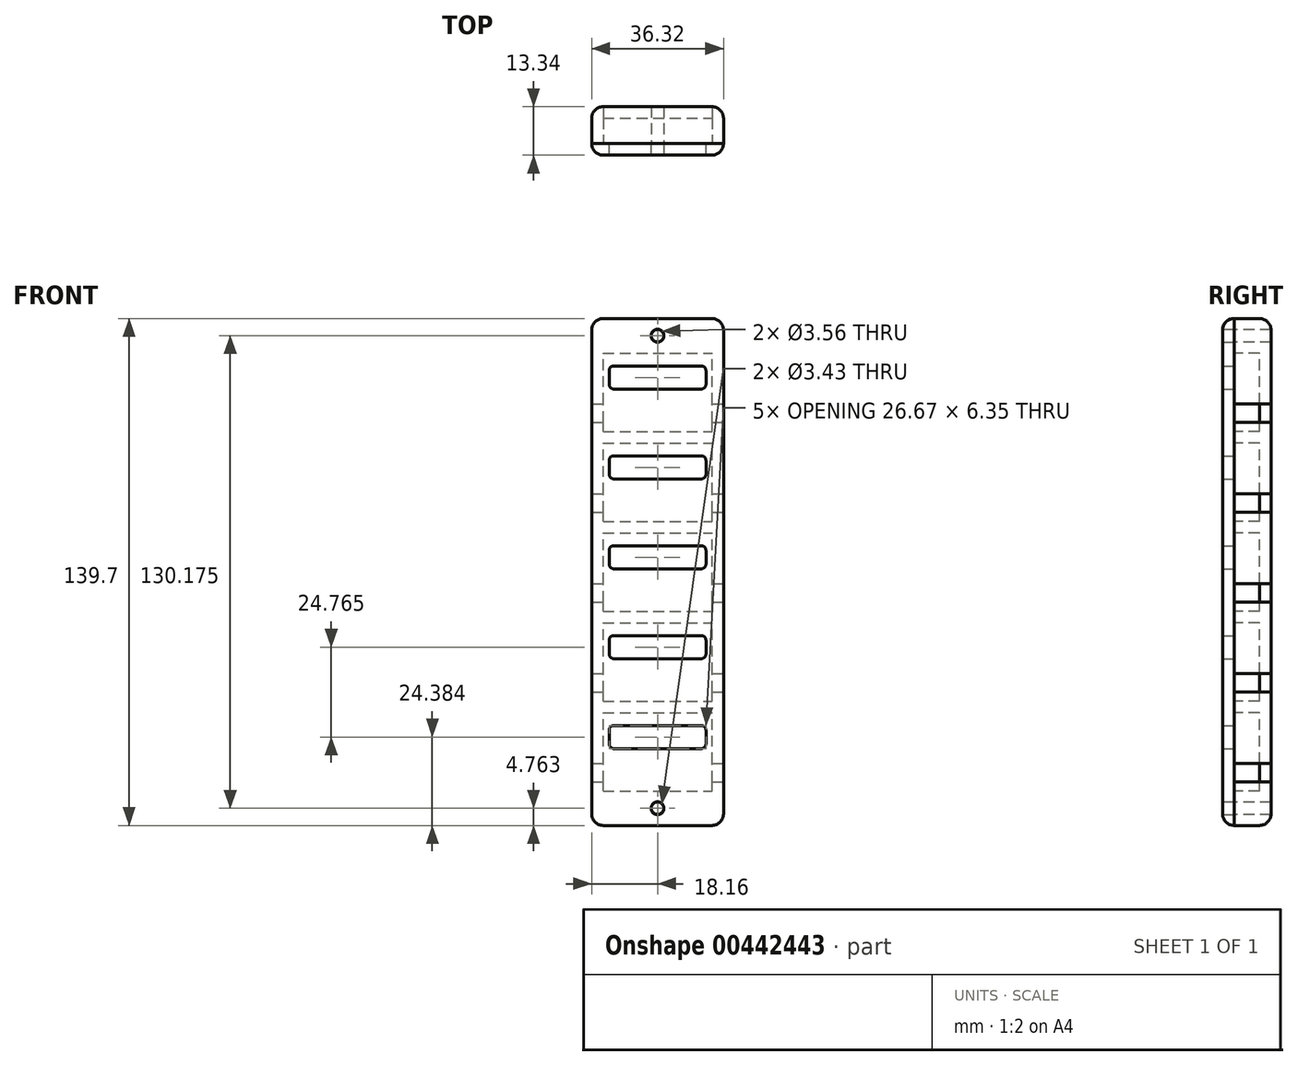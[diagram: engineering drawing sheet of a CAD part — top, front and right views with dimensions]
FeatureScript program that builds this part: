
annotation { "Feature Type Name" : "Feature", "Feature Type Description" : "" }
export const myFeature = defineFeature(function(context is Context, id is Id, definition is map)
    precondition{}
    {
        {
            var Q0;
            Q0=qCreatedBy(makeId("Front.planeOp"),FACE);
            var sketch = newSketch(context, id + "F0", { "sketchPlane" : qUnion([Q0])});
            skLineSegment(sketch, "E0.bottom", {"start": v(-18.16, 0) * mm, "end": v(18.16, 0) * mm});
            skLineSegment(sketch, "E0.top", {"start": v(-18.16, 139.7) * mm, "end": v(18.16, 139.7) * mm});
            skLineSegment(sketch, "E0.left", {"start": v(-18.16, 0) * mm, "end": v(-18.16, 139.7) * mm});
            skLineSegment(sketch, "E0.right", {"start": v(18.16, 0) * mm, "end": v(18.16, 139.7) * mm});
            skLineSegment(sketch, "E1.bottom", {"start": v(-14.99, 9.53) * mm, "end": v(14.99, 9.53) * mm});
            skLineSegment(sketch, "E1.top", {"start": v(-14.99, 31.12) * mm, "end": v(14.99, 31.12) * mm});
            skLineSegment(sketch, "E1.left", {"start": v(-14.99, 9.53) * mm, "end": v(-14.99, 31.12) * mm});
            skLineSegment(sketch, "E1.right", {"start": v(14.99, 9.53) * mm, "end": v(14.99, 31.12) * mm});
            skLineSegment(sketch, "E2.bottom", {"start": v(-14.99, 34.3) * mm, "end": v(14.99, 34.3) * mm});
            skLineSegment(sketch, "E2.top", {"start": v(-14.99, 55.88) * mm, "end": v(14.99, 55.88) * mm});
            skLineSegment(sketch, "E2.left", {"start": v(-14.99, 34.3) * mm, "end": v(-14.99, 55.88) * mm});
            skLineSegment(sketch, "E2.right", {"start": v(14.99, 34.3) * mm, "end": v(14.99, 55.88) * mm});
            skLineSegment(sketch, "E3.bottom", {"start": v(-14.99, 59.06) * mm, "end": v(14.99, 59.06) * mm});
            skLineSegment(sketch, "E3.top", {"start": v(-14.99, 80.65) * mm, "end": v(14.99, 80.65) * mm});
            skLineSegment(sketch, "E3.left", {"start": v(-14.99, 59.06) * mm, "end": v(-14.99, 80.65) * mm});
            skLineSegment(sketch, "E3.right", {"start": v(14.99, 59.06) * mm, "end": v(14.99, 80.65) * mm});
            skLineSegment(sketch, "E4.bottom", {"start": v(-14.99, 83.82) * mm, "end": v(14.99, 83.82) * mm});
            skLineSegment(sketch, "E4.top", {"start": v(-14.99, 105.41) * mm, "end": v(14.99, 105.41) * mm});
            skLineSegment(sketch, "E4.left", {"start": v(-14.99, 83.82) * mm, "end": v(-14.99, 105.41) * mm});
            skLineSegment(sketch, "E4.right", {"start": v(14.99, 83.82) * mm, "end": v(14.99, 105.41) * mm});
            skLineSegment(sketch, "E5.bottom", {"start": v(-14.99, 108.59) * mm, "end": v(14.99, 108.59) * mm});
            skLineSegment(sketch, "E5.top", {"start": v(-14.99, 130.18) * mm, "end": v(14.99, 130.18) * mm});
            skLineSegment(sketch, "E5.left", {"start": v(-14.99, 108.59) * mm, "end": v(-14.99, 130.18) * mm});
            skLineSegment(sketch, "E5.right", {"start": v(14.99, 108.59) * mm, "end": v(14.99, 130.18) * mm});
            skLineSegment(sketch, "E6", {"start": v(-18.16, 14.6) * mm, "end": v(18.16, 14.6) * mm, "construction": true});
            skLineSegment(sketch, "E7.bottom", {"start": v(-18.16, 12.06) * mm, "end": v(18.16, 12.06) * mm});
            skLineSegment(sketch, "E7.top", {"start": v(-18.16, 17.14) * mm, "end": v(18.16, 17.14) * mm});
            skLineSegment(sketch, "E7.left", {"start": v(-18.16, 12.06) * mm, "end": v(-18.16, 17.14) * mm});
            skLineSegment(sketch, "E7.right", {"start": v(18.16, 12.06) * mm, "end": v(18.16, 17.14) * mm});
            skLineSegment(sketch, "E8.0.1.0", {"start": v(-18.16, 36.83) * mm, "end": v(18.16, 36.83) * mm});
            skLineSegment(sketch, "E8.0.1.1", {"start": v(-18.16, 41.91) * mm, "end": v(18.16, 41.91) * mm});
            skLineSegment(sketch, "E8.0.1.2", {"start": v(18.16, 36.83) * mm, "end": v(18.16, 41.91) * mm});
            skLineSegment(sketch, "E8.0.1.3", {"start": v(-18.16, 39.37) * mm, "end": v(18.16, 39.37) * mm, "construction": true});
            skLineSegment(sketch, "E8.0.1.4", {"start": v(-18.16, 36.83) * mm, "end": v(-18.16, 41.91) * mm});
            skLineSegment(sketch, "E8.0.2.0", {"start": v(-18.16, 61.6) * mm, "end": v(18.16, 61.6) * mm});
            skLineSegment(sketch, "E8.0.2.1", {"start": v(-18.16, 66.67) * mm, "end": v(18.16, 66.67) * mm});
            skLineSegment(sketch, "E8.0.2.2", {"start": v(18.16, 61.6) * mm, "end": v(18.16, 66.67) * mm});
            skLineSegment(sketch, "E8.0.2.3", {"start": v(-18.16, 64.13) * mm, "end": v(18.16, 64.13) * mm, "construction": true});
            skLineSegment(sketch, "E8.0.2.4", {"start": v(-18.16, 61.6) * mm, "end": v(-18.16, 66.67) * mm});
            skLineSegment(sketch, "E8.0.3.0", {"start": v(-18.16, 86.36) * mm, "end": v(18.16, 86.36) * mm});
            skLineSegment(sketch, "E8.0.3.1", {"start": v(-18.16, 91.44) * mm, "end": v(18.16, 91.44) * mm});
            skLineSegment(sketch, "E8.0.3.2", {"start": v(18.16, 86.36) * mm, "end": v(18.16, 91.44) * mm});
            skLineSegment(sketch, "E8.0.3.3", {"start": v(-18.16, 88.9) * mm, "end": v(18.16, 88.9) * mm, "construction": true});
            skLineSegment(sketch, "E8.0.3.4", {"start": v(-18.16, 86.36) * mm, "end": v(-18.16, 91.44) * mm});
            skLineSegment(sketch, "E8.0.4.0", {"start": v(-18.16, 111.12) * mm, "end": v(18.16, 111.12) * mm});
            skLineSegment(sketch, "E8.0.4.1", {"start": v(-18.16, 116.2) * mm, "end": v(18.16, 116.2) * mm});
            skLineSegment(sketch, "E8.0.4.2", {"start": v(18.16, 111.12) * mm, "end": v(18.16, 116.2) * mm});
            skLineSegment(sketch, "E8.0.4.3", {"start": v(-18.16, 113.66) * mm, "end": v(18.16, 113.66) * mm, "construction": true});
            skLineSegment(sketch, "E8.0.4.4", {"start": v(-18.16, 111.12) * mm, "end": v(-18.16, 116.2) * mm});
            skLineSegment(sketch, "E8.direction1", {"start": v(-18.16, 12.06) * mm, "end": v(7.24, 12.06) * mm, "construction": true});
            skLineSegment(sketch, "E8.direction2", {"start": v(-18.16, 12.06) * mm, "end": v(-18.16, 36.83) * mm, "construction": true});
            skLineSegment(sketch, "E9", {"start": v(0, 139.7) * mm, "end": v(0, 130.18) * mm, "construction": true});
            skCircle(sketch, "E10", {"center": v(0, 134.94) * mm, "radius": 1.71 * mm});
            skLineSegment(sketch, "E11", {"start": v(0, 9.53) * mm, "end": v(0, 0) * mm, "construction": true});
            skCircle(sketch, "E12", {"center": v(0, 4.76) * mm, "radius": 1.71 * mm});
            skSolve(sketch);
        }
        {
            var Q0;
            {var subQ0=sQuery(id+"F0.wireOp",EDGE,"E7.bottom");var subQ1=sQuery(id+"F0.wireOp",EDGE,"E1.left");var subQ2=makeQuery(id+"F0.imprint","INTERSECT",VERTEX,{"derivedFrom":[subQ1,subQ0]});Q0=makeQuery(id+"F0.imprint","IMPRINT",FACE,{"disambiguationData":[TD([[makeQuery(id+"F0.imprint","IMPRINT",EDGE,{"disambiguationData":[TD([[subQ2,-1.0]])],"derivedFrom":subQ1}),-1.0]])]});}
            var Q1;
            {var subQ12=sQuery(id+"F0.wireOp",EDGE,"E3.top");Q1=makeQuery(id+"F0.imprint","IMPRINT",FACE,{"disambiguationData":[TD([[makeQuery(id+"F0.imprint","IMPRINT",EDGE,{"derivedFrom":subQ12}),1.0]])]});}
            var Q2;
            {var subQ0=sQuery(id+"F0.wireOp",EDGE,"E3.bottom");Q2=makeQuery(id+"F0.imprint","IMPRINT",FACE,{"disambiguationData":[TD([[makeQuery(id+"F0.imprint","IMPRINT",EDGE,{"derivedFrom":subQ0}),1.0]])]});}
            var Q3;
            {var subQ2=sQuery(id+"F0.wireOp",EDGE,"E0.bottom");Q3=makeQuery(id+"F0.imprint","IMPRINT",FACE,{"disambiguationData":[TD([[makeQuery(id+"F0.imprint","IMPRINT",EDGE,{"derivedFrom":subQ2}),1.0]])]});}
            var Q4;
            {var subQ0=sQuery(id+"F0.wireOp",EDGE,"E4.bottom");Q4=makeQuery(id+"F0.imprint","IMPRINT",FACE,{"disambiguationData":[TD([[makeQuery(id+"F0.imprint","IMPRINT",EDGE,{"derivedFrom":subQ0}),1.0]])]});}
            var Q5;
            {var subQ0=sQuery(id+"F0.wireOp",EDGE,"E4.top");Q5=makeQuery(id+"F0.imprint","IMPRINT",FACE,{"disambiguationData":[TD([[makeQuery(id+"F0.imprint","IMPRINT",EDGE,{"derivedFrom":subQ0}),-1.0]])]});}
            var Q6;
            {var subQ1=sQuery(id+"F0.wireOp",EDGE,"E0.top");Q6=makeQuery(id+"F0.imprint","IMPRINT",FACE,{"disambiguationData":[TD([[makeQuery(id+"F0.imprint","IMPRINT",EDGE,{"derivedFrom":subQ1}),-1.0]])]});}
            var Q7;
            {var subQ0=sQuery(id+"F0.wireOp",EDGE,"E2.top");Q7=makeQuery(id+"F0.imprint","IMPRINT",FACE,{"disambiguationData":[TD([[makeQuery(id+"F0.imprint","IMPRINT",EDGE,{"derivedFrom":subQ0}),-1.0]])]});}
            var Q8;
            {var subQ0=sQuery(id+"F0.wireOp",EDGE,"E1.bottom");Q8=makeQuery(id+"F0.imprint","IMPRINT",FACE,{"disambiguationData":[TD([[makeQuery(id+"F0.imprint","IMPRINT",EDGE,{"derivedFrom":subQ0}),1.0]])]});}
            var Q9;
            {var subQ5=sQuery(id+"F0.wireOp",EDGE,"E8.0.1.4");Q9=makeQuery(id+"F0.imprint","IMPRINT",FACE,{"disambiguationData":[TD([[makeQuery(id+"F0.imprint","IMPRINT",EDGE,{"derivedFrom":subQ5}),-1.0]])]});}
            var Q10;
            {var subQ0=sQuery(id+"F0.wireOp",EDGE,"E3.top");Q10=makeQuery(id+"F0.imprint","IMPRINT",FACE,{"disambiguationData":[TD([[makeQuery(id+"F0.imprint","IMPRINT",EDGE,{"derivedFrom":subQ0}),-1.0]])]});}
            var Q11;
            {var subQ5=sQuery(id+"F0.wireOp",EDGE,"E7.left");Q11=makeQuery(id+"F0.imprint","IMPRINT",FACE,{"disambiguationData":[TD([[makeQuery(id+"F0.imprint","IMPRINT",EDGE,{"derivedFrom":subQ5}),-1.0]])]});}
            var Q12;
            {var subQ0=sQuery(id+"F0.wireOp",EDGE,"E5.top");Q12=makeQuery(id+"F0.imprint","IMPRINT",FACE,{"disambiguationData":[TD([[makeQuery(id+"F0.imprint","IMPRINT",EDGE,{"derivedFrom":subQ0}),-1.0]])]});}
            var Q13;
            {var subQ0=sQuery(id+"F0.wireOp",EDGE,"E5.bottom");Q13=makeQuery(id+"F0.imprint","IMPRINT",FACE,{"disambiguationData":[TD([[makeQuery(id+"F0.imprint","IMPRINT",EDGE,{"derivedFrom":subQ0}),1.0]])]});}
            var Q14;
            {var subQ0=sQuery(id+"F0.wireOp",EDGE,"E1.top");Q14=makeQuery(id+"F0.imprint","IMPRINT",FACE,{"disambiguationData":[TD([[makeQuery(id+"F0.imprint","IMPRINT",EDGE,{"derivedFrom":subQ0}),-1.0]])]});}
            var Q15;
            {var subQ0=sQuery(id+"F0.wireOp",EDGE,"E2.bottom");Q15=makeQuery(id+"F0.imprint","IMPRINT",FACE,{"disambiguationData":[TD([[makeQuery(id+"F0.imprint","IMPRINT",EDGE,{"derivedFrom":subQ0}),1.0]])]});}
            var Q16;
            {var subQ5=sQuery(id+"F0.wireOp",EDGE,"E8.0.4.4");Q16=makeQuery(id+"F0.imprint","IMPRINT",FACE,{"disambiguationData":[TD([[makeQuery(id+"F0.imprint","IMPRINT",EDGE,{"derivedFrom":subQ5}),-1.0]])]});}
            var Q17;
            {var subQ5=sQuery(id+"F0.wireOp",EDGE,"E8.0.2.4");Q17=makeQuery(id+"F0.imprint","IMPRINT",FACE,{"disambiguationData":[TD([[makeQuery(id+"F0.imprint","IMPRINT",EDGE,{"derivedFrom":subQ5}),-1.0]])]});}
            var Q18;
            {var subQ0=sQuery(id+"F0.wireOp",EDGE,"E8.0.4.0");var subQ1=sQuery(id+"F0.wireOp",EDGE,"E5.left");var subQ2=makeQuery(id+"F0.imprint","INTERSECT",VERTEX,{"derivedFrom":[subQ1,subQ0]});Q18=makeQuery(id+"F0.imprint","IMPRINT",FACE,{"disambiguationData":[TD([[makeQuery(id+"F0.imprint","IMPRINT",EDGE,{"disambiguationData":[TD([[subQ2,-1.0]])],"derivedFrom":subQ1}),-1.0]])]});}
            var Q19;
            {var subQ12=sQuery(id+"F0.wireOp",EDGE,"E1.top");Q19=makeQuery(id+"F0.imprint","IMPRINT",FACE,{"disambiguationData":[TD([[makeQuery(id+"F0.imprint","IMPRINT",EDGE,{"derivedFrom":subQ12}),1.0]])]});}
            var Q20;
            {var subQ0=sQuery(id+"F0.wireOp",EDGE,"E8.0.1.0");var subQ1=sQuery(id+"F0.wireOp",EDGE,"E2.left");var subQ2=makeQuery(id+"F0.imprint","INTERSECT",VERTEX,{"derivedFrom":[subQ1,subQ0]});Q20=makeQuery(id+"F0.imprint","IMPRINT",FACE,{"disambiguationData":[TD([[makeQuery(id+"F0.imprint","IMPRINT",EDGE,{"disambiguationData":[TD([[subQ2,-1.0]])],"derivedFrom":subQ1}),-1.0]])]});}
            var Q21;
            {var subQ15=sQuery(id+"F0.wireOp",EDGE,"E4.top");Q21=makeQuery(id+"F0.imprint","IMPRINT",FACE,{"disambiguationData":[TD([[makeQuery(id+"F0.imprint","IMPRINT",EDGE,{"derivedFrom":subQ15}),1.0]])]});}
            var Q22;
            {var subQ5=sQuery(id+"F0.wireOp",EDGE,"E2.top");Q22=makeQuery(id+"F0.imprint","IMPRINT",FACE,{"disambiguationData":[TD([[makeQuery(id+"F0.imprint","IMPRINT",EDGE,{"derivedFrom":subQ5}),1.0]])]});}
            var Q23;
            {var subQ0=sQuery(id+"F0.wireOp",EDGE,"E8.0.2.0");var subQ1=sQuery(id+"F0.wireOp",EDGE,"E3.left");var subQ2=makeQuery(id+"F0.imprint","INTERSECT",VERTEX,{"derivedFrom":[subQ1,subQ0]});Q23=makeQuery(id+"F0.imprint","IMPRINT",FACE,{"disambiguationData":[TD([[makeQuery(id+"F0.imprint","IMPRINT",EDGE,{"disambiguationData":[TD([[subQ2,-1.0]])],"derivedFrom":subQ1}),-1.0]])]});}
            var Q24;
            {var subQ5=sQuery(id+"F0.wireOp",EDGE,"E8.0.3.4");Q24=makeQuery(id+"F0.imprint","IMPRINT",FACE,{"disambiguationData":[TD([[makeQuery(id+"F0.imprint","IMPRINT",EDGE,{"derivedFrom":subQ5}),-1.0]])]});}
            var Q25;
            {var subQ0=sQuery(id+"F0.wireOp",EDGE,"E8.0.3.0");var subQ1=sQuery(id+"F0.wireOp",EDGE,"E4.left");var subQ2=makeQuery(id+"F0.imprint","INTERSECT",VERTEX,{"derivedFrom":[subQ1,subQ0]});Q25=makeQuery(id+"F0.imprint","IMPRINT",FACE,{"disambiguationData":[TD([[makeQuery(id+"F0.imprint","IMPRINT",EDGE,{"disambiguationData":[TD([[subQ2,-1.0]])],"derivedFrom":subQ1}),-1.0]])]});}
            var Q26;
            {var subQ5=sQuery(id+"F0.wireOp",EDGE,"E8.0.1.2");Q26=makeQuery(id+"F0.imprint","IMPRINT",FACE,{"disambiguationData":[TD([[makeQuery(id+"F0.imprint","IMPRINT",EDGE,{"derivedFrom":subQ5}),1.0]])]});}
            var Q27;
            {var subQ5=sQuery(id+"F0.wireOp",EDGE,"E7.right");Q27=makeQuery(id+"F0.imprint","IMPRINT",FACE,{"disambiguationData":[TD([[makeQuery(id+"F0.imprint","IMPRINT",EDGE,{"derivedFrom":subQ5}),1.0]])]});}
            var Q28;
            {var subQ5=sQuery(id+"F0.wireOp",EDGE,"E8.0.3.2");Q28=makeQuery(id+"F0.imprint","IMPRINT",FACE,{"disambiguationData":[TD([[makeQuery(id+"F0.imprint","IMPRINT",EDGE,{"derivedFrom":subQ5}),1.0]])]});}
            var Q29;
            {var subQ5=sQuery(id+"F0.wireOp",EDGE,"E8.0.4.2");Q29=makeQuery(id+"F0.imprint","IMPRINT",FACE,{"disambiguationData":[TD([[makeQuery(id+"F0.imprint","IMPRINT",EDGE,{"derivedFrom":subQ5}),1.0]])]});}
            var Q30;
            {var subQ5=sQuery(id+"F0.wireOp",EDGE,"E8.0.2.2");Q30=makeQuery(id+"F0.imprint","IMPRINT",FACE,{"disambiguationData":[TD([[makeQuery(id+"F0.imprint","IMPRINT",EDGE,{"derivedFrom":subQ5}),1.0]])]});}
            extrude(context, id + "F1", {"entities" : qUnion([Q0, Q1, Q2, Q3, Q4, Q5, Q6, Q7, Q8, Q9, Q10, Q11, Q12, Q13, Q14, Q15, Q16, Q17, Q18, Q19, Q20, Q21, Q22, Q23, Q24, Q25, Q26, Q27, Q28, Q29, Q30]), "oppositeDirection" : true, "depth" : 10.16 * mm});
        }
        {
            var Q0;
            {var subQ0=sQuery(id+"F0.wireOp",EDGE,"E4.top");Q0=makeQuery(id+"F0.imprint","IMPRINT",FACE,{"disambiguationData":[TD([[makeQuery(id+"F0.imprint","IMPRINT",EDGE,{"derivedFrom":subQ0}),-1.0]])]});}
            var Q1;
            {var subQ0=sQuery(id+"F0.wireOp",EDGE,"E2.bottom");Q1=makeQuery(id+"F0.imprint","IMPRINT",FACE,{"disambiguationData":[TD([[makeQuery(id+"F0.imprint","IMPRINT",EDGE,{"derivedFrom":subQ0}),1.0]])]});}
            var Q2;
            {var subQ0=sQuery(id+"F0.wireOp",EDGE,"E2.top");Q2=makeQuery(id+"F0.imprint","IMPRINT",FACE,{"disambiguationData":[TD([[makeQuery(id+"F0.imprint","IMPRINT",EDGE,{"derivedFrom":subQ0}),-1.0]])]});}
            var Q3;
            {var subQ0=sQuery(id+"F0.wireOp",EDGE,"E8.0.2.0");var subQ1=sQuery(id+"F0.wireOp",EDGE,"E3.left");var subQ2=makeQuery(id+"F0.imprint","INTERSECT",VERTEX,{"derivedFrom":[subQ1,subQ0]});Q3=makeQuery(id+"F0.imprint","IMPRINT",FACE,{"disambiguationData":[TD([[makeQuery(id+"F0.imprint","IMPRINT",EDGE,{"disambiguationData":[TD([[subQ2,-1.0]])],"derivedFrom":subQ1}),-1.0]])]});}
            var Q4;
            {var subQ0=sQuery(id+"F0.wireOp",EDGE,"E7.bottom");var subQ1=sQuery(id+"F0.wireOp",EDGE,"E1.left");var subQ2=makeQuery(id+"F0.imprint","INTERSECT",VERTEX,{"derivedFrom":[subQ1,subQ0]});Q4=makeQuery(id+"F0.imprint","IMPRINT",FACE,{"disambiguationData":[TD([[makeQuery(id+"F0.imprint","IMPRINT",EDGE,{"disambiguationData":[TD([[subQ2,-1.0]])],"derivedFrom":subQ1}),-1.0]])]});}
            var Q5;
            {var subQ0=sQuery(id+"F0.wireOp",EDGE,"E1.bottom");Q5=makeQuery(id+"F0.imprint","IMPRINT",FACE,{"disambiguationData":[TD([[makeQuery(id+"F0.imprint","IMPRINT",EDGE,{"derivedFrom":subQ0}),1.0]])]});}
            var Q6;
            {var subQ0=sQuery(id+"F0.wireOp",EDGE,"E8.0.4.0");var subQ1=sQuery(id+"F0.wireOp",EDGE,"E5.left");var subQ2=makeQuery(id+"F0.imprint","INTERSECT",VERTEX,{"derivedFrom":[subQ1,subQ0]});Q6=makeQuery(id+"F0.imprint","IMPRINT",FACE,{"disambiguationData":[TD([[makeQuery(id+"F0.imprint","IMPRINT",EDGE,{"disambiguationData":[TD([[subQ2,-1.0]])],"derivedFrom":subQ1}),-1.0]])]});}
            var Q7;
            {var subQ0=sQuery(id+"F0.wireOp",EDGE,"E8.0.3.0");var subQ1=sQuery(id+"F0.wireOp",EDGE,"E4.left");var subQ2=makeQuery(id+"F0.imprint","INTERSECT",VERTEX,{"derivedFrom":[subQ1,subQ0]});Q7=makeQuery(id+"F0.imprint","IMPRINT",FACE,{"disambiguationData":[TD([[makeQuery(id+"F0.imprint","IMPRINT",EDGE,{"disambiguationData":[TD([[subQ2,-1.0]])],"derivedFrom":subQ1}),-1.0]])]});}
            var Q8;
            {var subQ0=sQuery(id+"F0.wireOp",EDGE,"E5.top");Q8=makeQuery(id+"F0.imprint","IMPRINT",FACE,{"disambiguationData":[TD([[makeQuery(id+"F0.imprint","IMPRINT",EDGE,{"derivedFrom":subQ0}),-1.0]])]});}
            var Q9;
            {var subQ0=sQuery(id+"F0.wireOp",EDGE,"E3.bottom");Q9=makeQuery(id+"F0.imprint","IMPRINT",FACE,{"disambiguationData":[TD([[makeQuery(id+"F0.imprint","IMPRINT",EDGE,{"derivedFrom":subQ0}),1.0]])]});}
            var Q10;
            {var subQ0=sQuery(id+"F0.wireOp",EDGE,"E1.top");Q10=makeQuery(id+"F0.imprint","IMPRINT",FACE,{"disambiguationData":[TD([[makeQuery(id+"F0.imprint","IMPRINT",EDGE,{"derivedFrom":subQ0}),-1.0]])]});}
            var Q11;
            {var subQ0=sQuery(id+"F0.wireOp",EDGE,"E3.top");Q11=makeQuery(id+"F0.imprint","IMPRINT",FACE,{"disambiguationData":[TD([[makeQuery(id+"F0.imprint","IMPRINT",EDGE,{"derivedFrom":subQ0}),-1.0]])]});}
            var Q12;
            {var subQ0=sQuery(id+"F0.wireOp",EDGE,"E8.0.1.0");var subQ1=sQuery(id+"F0.wireOp",EDGE,"E2.left");var subQ2=makeQuery(id+"F0.imprint","INTERSECT",VERTEX,{"derivedFrom":[subQ1,subQ0]});Q12=makeQuery(id+"F0.imprint","IMPRINT",FACE,{"disambiguationData":[TD([[makeQuery(id+"F0.imprint","IMPRINT",EDGE,{"disambiguationData":[TD([[subQ2,-1.0]])],"derivedFrom":subQ1}),-1.0]])]});}
            var Q13;
            {var subQ0=sQuery(id+"F0.wireOp",EDGE,"E4.bottom");Q13=makeQuery(id+"F0.imprint","IMPRINT",FACE,{"disambiguationData":[TD([[makeQuery(id+"F0.imprint","IMPRINT",EDGE,{"derivedFrom":subQ0}),1.0]])]});}
            var Q14;
            {var subQ0=sQuery(id+"F0.wireOp",EDGE,"E5.bottom");Q14=makeQuery(id+"F0.imprint","IMPRINT",FACE,{"disambiguationData":[TD([[makeQuery(id+"F0.imprint","IMPRINT",EDGE,{"derivedFrom":subQ0}),1.0]])]});}
            extrude(context, id + "F2", {"entities" : qUnion([Q0, Q1, Q2, Q3, Q4, Q5, Q6, Q7, Q8, Q9, Q10, Q11, Q12, Q13, Q14]), "operationType" : NewBodyOperationType.REMOVE, "oppositeDirection" : true, "depth" : 7 * mm});
        }
        {
            var Q0;
            {var subQ5=sQuery(id+"F0.wireOp",EDGE,"E7.left");Q0=makeQuery(id+"F0.imprint","IMPRINT",FACE,{"disambiguationData":[TD([[makeQuery(id+"F0.imprint","IMPRINT",EDGE,{"derivedFrom":subQ5}),-1.0]])]});}
            var Q1;
            {var subQ0=sQuery(id+"F0.wireOp",EDGE,"E7.bottom");var subQ1=sQuery(id+"F0.wireOp",EDGE,"E1.left");var subQ2=makeQuery(id+"F0.imprint","INTERSECT",VERTEX,{"derivedFrom":[subQ1,subQ0]});Q1=makeQuery(id+"F0.imprint","IMPRINT",FACE,{"disambiguationData":[TD([[makeQuery(id+"F0.imprint","IMPRINT",EDGE,{"disambiguationData":[TD([[subQ2,-1.0]])],"derivedFrom":subQ1}),-1.0]])]});}
            var Q2;
            {var subQ5=sQuery(id+"F0.wireOp",EDGE,"E7.right");Q2=makeQuery(id+"F0.imprint","IMPRINT",FACE,{"disambiguationData":[TD([[makeQuery(id+"F0.imprint","IMPRINT",EDGE,{"derivedFrom":subQ5}),1.0]])]});}
            var Q3;
            {var subQ5=sQuery(id+"F0.wireOp",EDGE,"E8.0.1.2");Q3=makeQuery(id+"F0.imprint","IMPRINT",FACE,{"disambiguationData":[TD([[makeQuery(id+"F0.imprint","IMPRINT",EDGE,{"derivedFrom":subQ5}),1.0]])]});}
            var Q4;
            {var subQ0=sQuery(id+"F0.wireOp",EDGE,"E8.0.1.0");var subQ1=sQuery(id+"F0.wireOp",EDGE,"E2.left");var subQ2=makeQuery(id+"F0.imprint","INTERSECT",VERTEX,{"derivedFrom":[subQ1,subQ0]});Q4=makeQuery(id+"F0.imprint","IMPRINT",FACE,{"disambiguationData":[TD([[makeQuery(id+"F0.imprint","IMPRINT",EDGE,{"disambiguationData":[TD([[subQ2,-1.0]])],"derivedFrom":subQ1}),-1.0]])]});}
            var Q5;
            {var subQ5=sQuery(id+"F0.wireOp",EDGE,"E8.0.1.4");Q5=makeQuery(id+"F0.imprint","IMPRINT",FACE,{"disambiguationData":[TD([[makeQuery(id+"F0.imprint","IMPRINT",EDGE,{"derivedFrom":subQ5}),-1.0]])]});}
            var Q6;
            {var subQ5=sQuery(id+"F0.wireOp",EDGE,"E8.0.3.4");Q6=makeQuery(id+"F0.imprint","IMPRINT",FACE,{"disambiguationData":[TD([[makeQuery(id+"F0.imprint","IMPRINT",EDGE,{"derivedFrom":subQ5}),-1.0]])]});}
            var Q7;
            {var subQ0=sQuery(id+"F0.wireOp",EDGE,"E8.0.3.0");var subQ1=sQuery(id+"F0.wireOp",EDGE,"E4.left");var subQ2=makeQuery(id+"F0.imprint","INTERSECT",VERTEX,{"derivedFrom":[subQ1,subQ0]});Q7=makeQuery(id+"F0.imprint","IMPRINT",FACE,{"disambiguationData":[TD([[makeQuery(id+"F0.imprint","IMPRINT",EDGE,{"disambiguationData":[TD([[subQ2,-1.0]])],"derivedFrom":subQ1}),-1.0]])]});}
            var Q8;
            {var subQ5=sQuery(id+"F0.wireOp",EDGE,"E8.0.3.2");Q8=makeQuery(id+"F0.imprint","IMPRINT",FACE,{"disambiguationData":[TD([[makeQuery(id+"F0.imprint","IMPRINT",EDGE,{"derivedFrom":subQ5}),1.0]])]});}
            var Q9;
            {var subQ5=sQuery(id+"F0.wireOp",EDGE,"E8.0.2.2");Q9=makeQuery(id+"F0.imprint","IMPRINT",FACE,{"disambiguationData":[TD([[makeQuery(id+"F0.imprint","IMPRINT",EDGE,{"derivedFrom":subQ5}),1.0]])]});}
            var Q10;
            {var subQ0=sQuery(id+"F0.wireOp",EDGE,"E8.0.2.0");var subQ1=sQuery(id+"F0.wireOp",EDGE,"E3.left");var subQ2=makeQuery(id+"F0.imprint","INTERSECT",VERTEX,{"derivedFrom":[subQ1,subQ0]});Q10=makeQuery(id+"F0.imprint","IMPRINT",FACE,{"disambiguationData":[TD([[makeQuery(id+"F0.imprint","IMPRINT",EDGE,{"disambiguationData":[TD([[subQ2,-1.0]])],"derivedFrom":subQ1}),-1.0]])]});}
            var Q11;
            {var subQ5=sQuery(id+"F0.wireOp",EDGE,"E8.0.2.4");Q11=makeQuery(id+"F0.imprint","IMPRINT",FACE,{"disambiguationData":[TD([[makeQuery(id+"F0.imprint","IMPRINT",EDGE,{"derivedFrom":subQ5}),-1.0]])]});}
            var Q12;
            {var subQ5=sQuery(id+"F0.wireOp",EDGE,"E8.0.4.4");Q12=makeQuery(id+"F0.imprint","IMPRINT",FACE,{"disambiguationData":[TD([[makeQuery(id+"F0.imprint","IMPRINT",EDGE,{"derivedFrom":subQ5}),-1.0]])]});}
            var Q13;
            {var subQ0=sQuery(id+"F0.wireOp",EDGE,"E8.0.4.0");var subQ1=sQuery(id+"F0.wireOp",EDGE,"E5.left");var subQ2=makeQuery(id+"F0.imprint","INTERSECT",VERTEX,{"derivedFrom":[subQ1,subQ0]});Q13=makeQuery(id+"F0.imprint","IMPRINT",FACE,{"disambiguationData":[TD([[makeQuery(id+"F0.imprint","IMPRINT",EDGE,{"disambiguationData":[TD([[subQ2,-1.0]])],"derivedFrom":subQ1}),-1.0]])]});}
            var Q14;
            {var subQ5=sQuery(id+"F0.wireOp",EDGE,"E8.0.4.2");Q14=makeQuery(id+"F0.imprint","IMPRINT",FACE,{"disambiguationData":[TD([[makeQuery(id+"F0.imprint","IMPRINT",EDGE,{"derivedFrom":subQ5}),1.0]])]});}
            extrude(context, id + "F3", {"entities" : qUnion([Q0, Q1, Q2, Q3, Q4, Q5, Q6, Q7, Q8, Q9, Q10, Q11, Q12, Q13, Q14]), "operationType" : NewBodyOperationType.REMOVE, "oppositeDirection" : true, "depth" : 1.9 * mm});
        }
        {
            var Q0;
            Q0=makeQuery(id+"F1.opExtrude","CAP_EDGE",EDGE,{"disambiguationData":[OSD([sQuery(id+"F0.wireOp",EDGE,"E0.right"),sQuery(id+"F0.wireOp",EDGE,"E7.right"),sQuery(id+"F0.wireOp",EDGE,"E8.0.1.2"),sQuery(id+"F0.wireOp",EDGE,"E8.0.2.2"),sQuery(id+"F0.wireOp",EDGE,"E8.0.3.2"),sQuery(id+"F0.wireOp",EDGE,"E8.0.4.2")])],"isStart":false});
            var Q1;
            Q1=makeQuery(id+"F1.opExtrude","CAP_EDGE",EDGE,{"disambiguationData":[OSD([sQuery(id+"F0.wireOp",EDGE,"E0.left"),sQuery(id+"F0.wireOp",EDGE,"E7.left"),sQuery(id+"F0.wireOp",EDGE,"E8.0.1.4"),sQuery(id+"F0.wireOp",EDGE,"E8.0.2.4"),sQuery(id+"F0.wireOp",EDGE,"E8.0.3.4"),sQuery(id+"F0.wireOp",EDGE,"E8.0.4.4")])],"isStart":false});
            var Q2;
            Q2=makeQuery(id+"F1.opExtrude","SWEPT_EDGE",EDGE,{"disambiguationData":[OSD([sQuery(id+"F0.wireOp",EDGE,"E0.top"),sQuery(id+"F0.wireOp",EDGE,"E0.right")])]});
            var Q3;
            Q3=makeQuery(id+"F1.opExtrude","SWEPT_EDGE",EDGE,{"disambiguationData":[OSD([sQuery(id+"F0.wireOp",EDGE,"E0.top"),sQuery(id+"F0.wireOp",EDGE,"E0.left")])]});
            var Q4;
            Q4=makeQuery(id+"F1.opExtrude","SWEPT_EDGE",EDGE,{"disambiguationData":[OSD([sQuery(id+"F0.wireOp",EDGE,"E0.bottom"),sQuery(id+"F0.wireOp",EDGE,"E0.left")])]});
            var Q5;
            Q5=makeQuery(id+"F1.opExtrude","SWEPT_EDGE",EDGE,{"disambiguationData":[OSD([sQuery(id+"F0.wireOp",EDGE,"E0.bottom"),sQuery(id+"F0.wireOp",EDGE,"E0.right")])]});
            var Q6;
            Q6=makeQuery(id+"F1.opExtrude","CAP_EDGE",EDGE,{"disambiguationData":[OSD([sQuery(id+"F0.wireOp",EDGE,"E0.bottom")])],"isStart":false});
            var Q7;
            Q7=makeQuery(id+"F1.opExtrude","CAP_EDGE",EDGE,{"disambiguationData":[OSD([sQuery(id+"F0.wireOp",EDGE,"E0.top")])],"isStart":false});
            fillet(context, id + "F4", {"entities" : qUnion([Q0, Q1, Q2, Q3, Q4, Q5, Q6, Q7]), "radius" : 3.17 * mm, "tangentPropagation" : true, "allowEdgeOverflow" : false});
        }
        {
            var Q0;
            Q0=qCreatedBy(makeId("Front.planeOp"),FACE);
            var sketch = newSketch(context, id + "F5", { "sketchPlane" : qUnion([Q0])});
            skLineSegment(sketch, "E13.bottom", {"start": v(-14.99, 0) * mm, "end": v(14.99, 0) * mm});
            skLineSegment(sketch, "E13.top", {"start": v(-14.99, 139.7) * mm, "end": v(14.99, 139.7) * mm});
            skLineSegment(sketch, "E13.left", {"start": v(-18.16, 3.17) * mm, "end": v(-18.16, 136.53) * mm});
            skLineSegment(sketch, "E13.right", {"start": v(18.16, 3.17) * mm, "end": v(18.16, 136.53) * mm});
            skPoint(sketch, "E14.visualSharp", {"position": v(18.16, 139.7) * mm});
            skArc(sketch, "E14.filletArc", {"start": v(18.16, 136.53) * mm, "mid": v(17.23, 138.77) * mm, "end": v(14.99, 139.7) * mm});
            skPoint(sketch, "E15.visualSharp", {"position": v(-18.16, 139.7) * mm});
            skArc(sketch, "E15.filletArc", {"start": v(-14.99, 139.7) * mm, "mid": v(-17.23, 138.77) * mm, "end": v(-18.16, 136.53) * mm});
            skPoint(sketch, "E16.visualSharp", {"position": v(-18.16, 0) * mm});
            skArc(sketch, "E16.filletArc", {"start": v(-18.16, 3.17) * mm, "mid": v(-17.23, 0.93) * mm, "end": v(-14.99, 0) * mm});
            skPoint(sketch, "E17.visualSharp", {"position": v(18.16, 0) * mm});
            skArc(sketch, "E17.filletArc", {"start": v(14.99, 0) * mm, "mid": v(17.23, 0.93) * mm, "end": v(18.16, 3.17) * mm});
            skLineSegment(sketch, "E18", {"start": v(-18.16, 24.38) * mm, "end": v(18.16, 24.38) * mm, "construction": true});
            skLineSegment(sketch, "E19.bottom", {"start": v(-12.06, 21.2) * mm, "end": v(12.07, 21.2) * mm});
            skLineSegment(sketch, "E19.top", {"start": v(-12.06, 27.56) * mm, "end": v(12.06, 27.56) * mm});
            skLineSegment(sketch, "E19.left", {"start": v(-13.34, 22.48) * mm, "end": v(-13.34, 26.29) * mm});
            skLineSegment(sketch, "E19.right", {"start": v(13.34, 22.48) * mm, "end": v(13.34, 26.29) * mm});
            skPoint(sketch, "E20.visualSharp", {"position": v(13.33, 27.56) * mm});
            skArc(sketch, "E20.filletArc", {"start": v(13.33, 26.29) * mm, "mid": v(12.96, 27.19) * mm, "end": v(12.06, 27.56) * mm});
            skPoint(sketch, "E21.visualSharp", {"position": v(-13.33, 27.56) * mm});
            skArc(sketch, "E21.filletArc", {"start": v(-12.06, 27.56) * mm, "mid": v(-12.96, 27.19) * mm, "end": v(-13.33, 26.29) * mm});
            skPoint(sketch, "E22.visualSharp", {"position": v(-13.33, 21.2) * mm});
            skArc(sketch, "E22.filletArc", {"start": v(-13.33, 22.48) * mm, "mid": v(-12.96, 21.58) * mm, "end": v(-12.06, 21.2) * mm});
            skPoint(sketch, "E23.visualSharp", {"position": v(13.33, 21.2) * mm});
            skArc(sketch, "E23.filletArc", {"start": v(12.07, 21.2) * mm, "mid": v(12.96, 21.58) * mm, "end": v(13.33, 22.48) * mm});
            skLineSegment(sketch, "E24.0.1.0", {"start": v(-12.06, 45.97) * mm, "end": v(12.07, 45.97) * mm});
            skPoint(sketch, "E24.0.1.1", {"position": v(13.33, 52.32) * mm});
            skPoint(sketch, "E24.0.1.2", {"position": v(-13.33, 52.32) * mm});
            skLineSegment(sketch, "E24.0.1.3", {"start": v(-12.06, 52.32) * mm, "end": v(12.06, 52.32) * mm});
            skLineSegment(sketch, "E24.0.1.4", {"start": v(-13.34, 47.24) * mm, "end": v(-13.34, 51.05) * mm});
            skLineSegment(sketch, "E24.0.1.5", {"start": v(13.34, 47.24) * mm, "end": v(13.34, 51.05) * mm});
            skPoint(sketch, "E24.0.1.6", {"position": v(13.33, 45.97) * mm});
            skPoint(sketch, "E24.0.1.7", {"position": v(-13.33, 45.97) * mm});
            skArc(sketch, "E24.0.1.8", {"start": v(-13.33, 47.24) * mm, "mid": v(-12.96, 46.35) * mm, "end": v(-12.06, 45.97) * mm});
            skArc(sketch, "E24.0.1.9", {"start": v(-12.06, 52.32) * mm, "mid": v(-12.96, 51.95) * mm, "end": v(-13.33, 51.05) * mm});
            skArc(sketch, "E24.0.1.10", {"start": v(13.33, 51.05) * mm, "mid": v(12.96, 51.95) * mm, "end": v(12.06, 52.32) * mm});
            skArc(sketch, "E24.0.1.11", {"start": v(12.07, 45.97) * mm, "mid": v(12.96, 46.35) * mm, "end": v(13.33, 47.24) * mm});
            skLineSegment(sketch, "E24.0.2.0", {"start": v(-12.06, 70.74) * mm, "end": v(12.07, 70.74) * mm});
            skPoint(sketch, "E24.0.2.1", {"position": v(13.33, 77.09) * mm});
            skPoint(sketch, "E24.0.2.2", {"position": v(-13.33, 77.09) * mm});
            skLineSegment(sketch, "E24.0.2.3", {"start": v(-12.06, 77.09) * mm, "end": v(12.06, 77.09) * mm});
            skLineSegment(sketch, "E24.0.2.4", {"start": v(-13.34, 72) * mm, "end": v(-13.34, 75.82) * mm});
            skLineSegment(sketch, "E24.0.2.5", {"start": v(13.34, 72) * mm, "end": v(13.34, 75.82) * mm});
            skPoint(sketch, "E24.0.2.6", {"position": v(13.33, 70.74) * mm});
            skPoint(sketch, "E24.0.2.7", {"position": v(-13.33, 70.74) * mm});
            skArc(sketch, "E24.0.2.8", {"start": v(-13.33, 72) * mm, "mid": v(-12.96, 71.11) * mm, "end": v(-12.06, 70.74) * mm});
            skArc(sketch, "E24.0.2.9", {"start": v(-12.06, 77.09) * mm, "mid": v(-12.96, 76.72) * mm, "end": v(-13.33, 75.82) * mm});
            skArc(sketch, "E24.0.2.10", {"start": v(13.33, 75.82) * mm, "mid": v(12.96, 76.72) * mm, "end": v(12.06, 77.09) * mm});
            skArc(sketch, "E24.0.2.11", {"start": v(12.07, 70.74) * mm, "mid": v(12.96, 71.11) * mm, "end": v(13.33, 72) * mm});
            skLineSegment(sketch, "E24.0.3.0", {"start": v(-12.06, 95.5) * mm, "end": v(12.07, 95.5) * mm});
            skPoint(sketch, "E24.0.3.1", {"position": v(13.33, 101.85) * mm});
            skPoint(sketch, "E24.0.3.2", {"position": v(-13.33, 101.85) * mm});
            skLineSegment(sketch, "E24.0.3.3", {"start": v(-12.06, 101.85) * mm, "end": v(12.06, 101.85) * mm});
            skLineSegment(sketch, "E24.0.3.4", {"start": v(-13.34, 96.77) * mm, "end": v(-13.34, 100.58) * mm});
            skLineSegment(sketch, "E24.0.3.5", {"start": v(13.34, 96.77) * mm, "end": v(13.34, 100.58) * mm});
            skPoint(sketch, "E24.0.3.6", {"position": v(13.33, 95.5) * mm});
            skPoint(sketch, "E24.0.3.7", {"position": v(-13.33, 95.5) * mm});
            skArc(sketch, "E24.0.3.8", {"start": v(-13.33, 96.77) * mm, "mid": v(-12.96, 95.88) * mm, "end": v(-12.06, 95.5) * mm});
            skArc(sketch, "E24.0.3.9", {"start": v(-12.06, 101.85) * mm, "mid": v(-12.96, 101.48) * mm, "end": v(-13.33, 100.58) * mm});
            skArc(sketch, "E24.0.3.10", {"start": v(13.33, 100.58) * mm, "mid": v(12.96, 101.48) * mm, "end": v(12.06, 101.85) * mm});
            skArc(sketch, "E24.0.3.11", {"start": v(12.07, 95.5) * mm, "mid": v(12.96, 95.88) * mm, "end": v(13.33, 96.77) * mm});
            skLineSegment(sketch, "E24.0.4.0", {"start": v(-12.06, 120.27) * mm, "end": v(12.07, 120.27) * mm});
            skPoint(sketch, "E24.0.4.1", {"position": v(13.33, 126.62) * mm});
            skPoint(sketch, "E24.0.4.2", {"position": v(-13.33, 126.62) * mm});
            skLineSegment(sketch, "E24.0.4.3", {"start": v(-12.06, 126.62) * mm, "end": v(12.06, 126.62) * mm});
            skLineSegment(sketch, "E24.0.4.4", {"start": v(-13.34, 121.54) * mm, "end": v(-13.34, 125.35) * mm});
            skLineSegment(sketch, "E24.0.4.5", {"start": v(13.34, 121.54) * mm, "end": v(13.34, 125.35) * mm});
            skPoint(sketch, "E24.0.4.6", {"position": v(13.33, 120.27) * mm});
            skPoint(sketch, "E24.0.4.7", {"position": v(-13.33, 120.27) * mm});
            skArc(sketch, "E24.0.4.8", {"start": v(-13.33, 121.54) * mm, "mid": v(-12.96, 120.64) * mm, "end": v(-12.06, 120.27) * mm});
            skArc(sketch, "E24.0.4.9", {"start": v(-12.06, 126.62) * mm, "mid": v(-12.96, 126.25) * mm, "end": v(-13.33, 125.35) * mm});
            skArc(sketch, "E24.0.4.10", {"start": v(13.33, 125.35) * mm, "mid": v(12.96, 126.25) * mm, "end": v(12.06, 126.62) * mm});
            skArc(sketch, "E24.0.4.11", {"start": v(12.07, 120.27) * mm, "mid": v(12.96, 120.64) * mm, "end": v(13.33, 121.54) * mm});
            skLineSegment(sketch, "E24.direction1", {"start": v(-13.33, 21.2) * mm, "end": v(12.06, 21.2) * mm, "construction": true});
            skLineSegment(sketch, "E24.direction2", {"start": v(-13.33, 21.2) * mm, "end": v(-13.33, 45.97) * mm, "construction": true});
            skCircle(sketch, "E25", {"center": v(0, 134.94) * mm, "radius": 1.78 * mm});
            skCircle(sketch, "E26", {"center": v(0, 4.76) * mm, "radius": 1.78 * mm});
            skSolve(sketch);
        }
        {
            var Q0;
            Q0=makeQuery(id+"F5.imprint","IMPRINT",FACE,{"disambiguationData":[TD([[makeQuery(id+"F5.imprint","IMPRINT",EDGE,{"derivedFrom":sQuery(id+"F5.wireOp",EDGE,"E13.bottom")}),1.0]])]});
            extrude(context, id + "F6", {"entities" : qUnion([Q0]), "depth" : 3.17 * mm});
        }
        {
            var Q0;
            Q0=makeQuery(id+"F6.opExtrude","CAP_EDGE",EDGE,{"disambiguationData":[OSD([sQuery(id+"F5.wireOp",EDGE,"E13.right")])],"isStart":false});
            fillet(context, id + "F7", {"entities" : qUnion([Q0]), "radius" : 3.17 * mm, "tangentPropagation" : true, "allowEdgeOverflow" : false});
        }
    });
